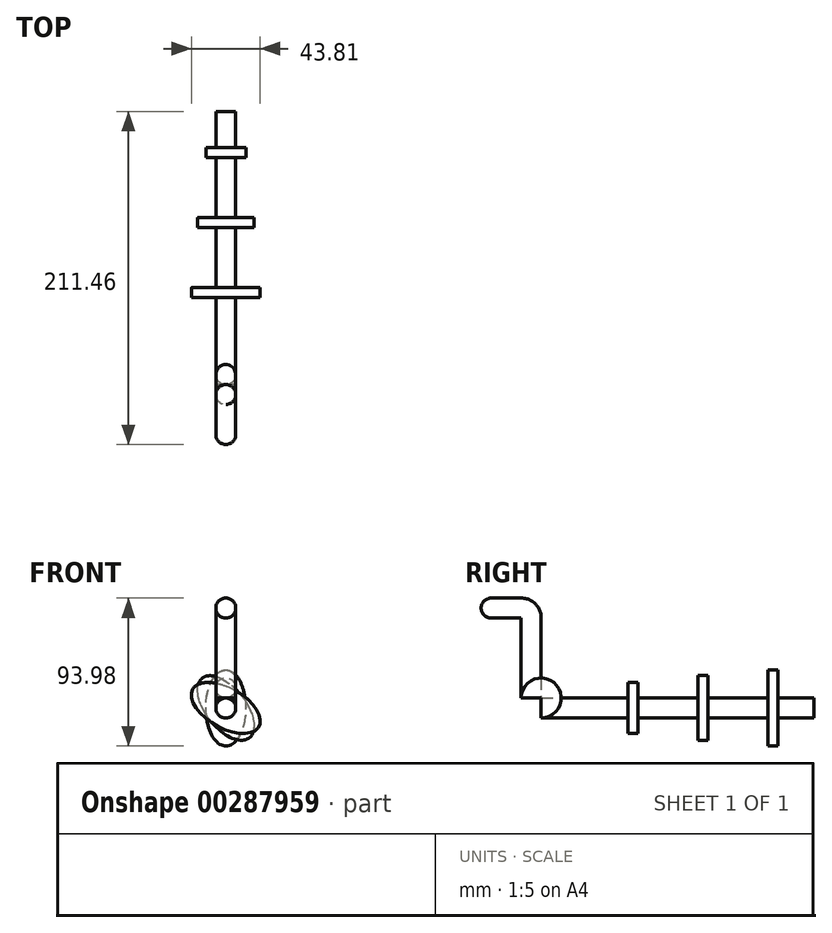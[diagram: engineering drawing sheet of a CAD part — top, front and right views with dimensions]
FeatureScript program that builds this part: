
annotation { "Feature Type Name" : "Feature", "Feature Type Description" : "" }
export const myFeature = defineFeature(function(context is Context, id is Id, definition is map)
    precondition{}
    {
        {
            var Q0;
            Q0=qCreatedBy(makeId("Front.planeOp"),FACE);
            var sketch = newSketch(context, id + "F0", { "sketchPlane" : qUnion([Q0])});
            skCircle(sketch, "E0", {"center": v(-40.6, -12.22) * mm, "radius": 6.35 * mm});
            skSolve(sketch);
        }
        {
            var Q0;
            Q0 = qSketchRegion(id + "F0", true);
            extrude(context, id + "F1", {"entities" : qUnion([Q0]), "depth" : 179.07 * mm});
        }
        {
            var Q0;
            Q0=makeQuery(id+"F1.opExtrude","CAP_EDGE",EDGE,{"disambiguationData":[OSD([sQuery(id+"F0.wireOp",EDGE,"E0")])],"isStart":false});
            cPlane(context, id + "F2", {"entities" : qUnion([Q0]), "cplaneType" : CPlaneType.LINE_ANGLE, "offset" : 0 * mm, "angle" : 0 * degree, "width" : 152.4 * mm, "height" : 152.4 * mm});
        }
        {
            var Q0;
            Q0=qCreatedBy(id+"F2.planeOp",FACE);
            cPlane(context, id + "F3", {"entities" : qUnion([Q0]), "cplaneType" : CPlaneType.OFFSET, "offset" : 6.35 * mm, "oppositeDirection" : true, "width" : 152.4 * mm, "height" : 152.4 * mm});
        }
        {
            var Q0;
            Q0=qCreatedBy(id+"F3.planeOp",FACE);
            var sketch = newSketch(context, id + "F4", { "sketchPlane" : qUnion([Q0])});
            skLineSegment(sketch, "E1", {"start": v(-64.8, 179.07) * mm, "end": v(-17.86, 179.07) * mm, "construction": true});
            skSolve(sketch);
        }
        {
            var Q0;
            Q0=makeQuery(id+"F1.opExtrude","CAP_FACE",FACE,{"disambiguationData":[OSD([sQuery(id+"F0.wireOp",EDGE,"E0")])],"isStart":false});
            var Q1;
            Q1=sQuery(id+"F4.wireOp",EDGE,"E1");
            revolve(context, id + "F5", {"operationType" : NewBodyOperationType.ADD, "entities" : qUnion([Q0]), "axis" : qUnion([Q1]), "revolveType" : RevolveType.ONE_DIRECTION, "oppositeDirection" : true, "angle" : 90 * degree});
        }
        {
            var Q0;
            Q0=makeQuery(id+"F5.opRevolve","CAP_FACE",FACE,{"disambiguationData":[OSD([sQuery(id+"F0.wireOp",EDGE,"E0")])],"isStart":false});
            extrude(context, id + "F6", {"entities" : qUnion([Q0]), "operationType" : NewBodyOperationType.ADD, "depth" : 50.8 * mm});
        }
        {
            var Q0;
            Q0=makeQuery(id+"F6.opExtrude","CAP_FACE",FACE,{"disambiguationData":[OSD([sQuery(id+"F0.wireOp",EDGE,"E0")])],"isStart":false});
            var sketch = newSketch(context, id + "F7", { "sketchPlane" : qUnion([Q0])});
            skLineSegment(sketch, "E2", {"start": v(-61.65, -185.42) * mm, "end": v(-16.9, -185.42) * mm, "construction": true});
            skLineSegment(sketch, "E3", {"start": v(-61.06, -191.77) * mm, "end": v(-25.87, -191.77) * mm, "construction": true});
            skSolve(sketch);
        }
        {
            var Q0;
            Q0=makeQuery(id+"F7.imprint","IMPRINT",FACE,{"disambiguationData":[TD([[makeQuery(id+"F7.imprint","IMPRINT",EDGE,{"derivedFrom":makeQuery(id+"F6.opExtrude","CAP_EDGE",EDGE,{"disambiguationData":[OSD([sQuery(id+"F0.wireOp",EDGE,"E0")])],"isStart":false})}),1.0]])]});
            var Q1;
            Q1=sQuery(id+"F7.wireOp",EDGE,"E3");
            revolve(context, id + "F8", {"operationType" : NewBodyOperationType.ADD, "entities" : qUnion([Q0]), "axis" : qUnion([Q1]), "revolveType" : RevolveType.ONE_DIRECTION, "angle" : 90 * degree});
        }
        {
            var Q0;
            Q0=makeQuery(id+"F8.opRevolve","CAP_FACE",FACE,{"disambiguationData":[OSD([sQuery(id+"F0.wireOp",EDGE,"E0")])],"isStart":false});
            extrude(context, id + "F9", {"entities" : qUnion([Q0]), "operationType" : NewBodyOperationType.ADD, "depth" : 25.4 * mm});
        }
        {
            var Q0;
            Q0=makeQuery(id+"F9.opExtrude","CAP_EDGE",EDGE,{"disambiguationData":[OSD([sQuery(id+"F0.wireOp",EDGE,"E0")])],"isStart":false});
            fillet(context, id + "F10", {"entities" : qUnion([Q0]), "radius" : 6.35 * mm, "tangentPropagation" : true, "allowEdgeOverflow" : false});
        }
        {
            var Q0;
            Q0=makeQuery(id+"F1.opExtrude","CAP_FACE",FACE,{"disambiguationData":[OSD([sQuery(id+"F0.wireOp",EDGE,"E0")])],"isStart":true});
            cPlane(context, id + "F11", {"entities" : qUnion([Q0]), "cplaneType" : CPlaneType.OFFSET, "offset" : 76.2 * mm, "oppositeDirection" : true, "width" : 152.4 * mm, "height" : 152.4 * mm});
        }
        {
            var Q0;
            Q0=qCreatedBy(id+"F11.planeOp",FACE);
            cPlane(context, id + "F12", {"entities" : qUnion([Q0]), "cplaneType" : CPlaneType.OFFSET, "offset" : 44.45 * mm, "width" : 152.4 * mm, "height" : 152.4 * mm});
        }
        {
            var Q0;
            Q0=qCreatedBy(id+"F11.planeOp",FACE);
            cPlane(context, id + "F13", {"entities" : qUnion([Q0]), "cplaneType" : CPlaneType.OFFSET, "offset" : 44.45 * mm, "oppositeDirection" : true, "width" : 152.4 * mm, "height" : 152.4 * mm});
        }
        {
            var Q0;
            Q0=qCreatedBy(id+"F13.planeOp",FACE);
            var sketch = newSketch(context, id + "F14", { "sketchPlane" : qUnion([Q0])});
            skEllipse(sketch, "E4", {"center": v(40.6, -12.22) * mm, "majorRadius": 24.13 * mm, "minorRadius": 12.7 * mm, "majorAxis": v(0.87, 0.5)});
            skSolve(sketch);
        }
        {
            var Q0;
            Q0=qCreatedBy(id+"F12.planeOp",FACE);
            var sketch = newSketch(context, id + "F15", { "sketchPlane" : qUnion([Q0])});
            skEllipse(sketch, "E5", {"center": v(40.6, -12.22) * mm, "majorRadius": 24.13 * mm, "minorRadius": 12.7 * mm, "majorAxis": v(0, 1)});
            skSolve(sketch);
        }
        {
            var Q0;
            Q0=qCreatedBy(id+"F11.planeOp",FACE);
            var sketch = newSketch(context, id + "F16", { "sketchPlane" : qUnion([Q0])});
            skEllipse(sketch, "E6", {"center": v(40.6, -12.22) * mm, "majorRadius": 24.13 * mm, "minorRadius": 12.7 * mm, "majorAxis": v(0.62, 0.79)});
            skSolve(sketch);
        }
        {
            var Q0;
            Q0=makeQuery(id+"F14.imprint","IMPRINT",FACE,{"disambiguationData":[TD([[makeQuery(id+"F14.imprint","IMPRINT",EDGE,{"derivedFrom":sQuery(id+"F14.wireOp",EDGE,"E4")}),1.0]])]});
            var Q1;
            Q1=makeQuery(id+"F16.imprint","IMPRINT",FACE,{"disambiguationData":[TD([[makeQuery(id+"F16.imprint","IMPRINT",EDGE,{"derivedFrom":sQuery(id+"F16.wireOp",EDGE,"E6")}),1.0]])]});
            var Q2;
            Q2=makeQuery(id+"F15.imprint","IMPRINT",FACE,{"disambiguationData":[TD([[makeQuery(id+"F15.imprint","IMPRINT",EDGE,{"derivedFrom":sQuery(id+"F15.wireOp",EDGE,"E5")}),1.0]])]});
            extrude(context, id + "F17", {"entities" : qUnion([Q0, Q1, Q2]), "operationType" : NewBodyOperationType.ADD, "endBound" : BoundingType.SYMMETRIC, "depth" : 6.35 * mm});
        }
        {
            var Q0;
            Q0=makeQuery(id+"F1.opExtrude","CAP_FACE",FACE,{"disambiguationData":[OSD([sQuery(id+"F0.wireOp",EDGE,"E0")])],"isStart":true});
            extrude(context, id + "F18", {"entities" : qUnion([Q0]), "operationType" : NewBodyOperationType.REMOVE, "oppositeDirection" : true, "depth" : 5.7 * mm});
        }
    });
